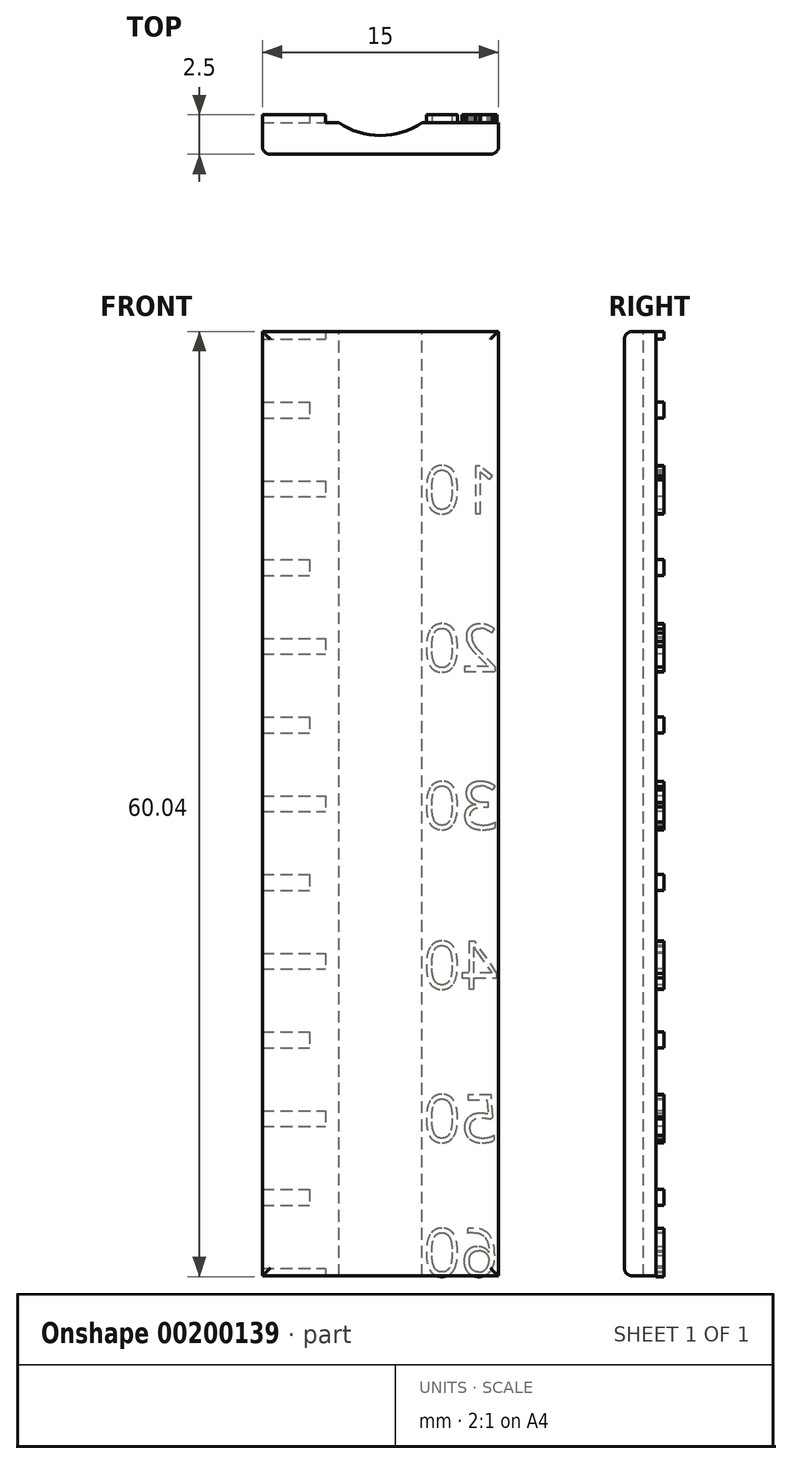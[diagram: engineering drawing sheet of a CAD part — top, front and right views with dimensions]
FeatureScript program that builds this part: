
annotation { "Feature Type Name" : "Feature", "Feature Type Description" : "" }
export const myFeature = defineFeature(function(context is Context, id is Id, definition is map)
    precondition{}
    {
        {
            var Q0;
            Q0=qCreatedBy(makeId("Top.planeOp"),FACE);
            var sketch = newSketch(context, id + "F0", { "sketchPlane" : qUnion([Q0])});
            skLineSegment(sketch, "E0.bottom", {"start": v(0, 0) * mm, "end": v(15, 0) * mm});
            skLineSegment(sketch, "E0.top", {"start": v(0, 2) * mm, "end": v(4.85, 2) * mm});
            skLineSegment(sketch, "E0.left", {"start": v(0, 0) * mm, "end": v(0, 2) * mm});
            skLineSegment(sketch, "E0.right", {"start": v(15, 0) * mm, "end": v(15, 2) * mm});
            skLineSegment(sketch, "E1", {"start": v(7.5, 2) * mm, "end": v(7.5, 5.94) * mm, "construction": true});
            skArc(sketch, "E2", {"start": v(4.85, 2) * mm, "mid": v(7.5, 1.2) * mm, "end": v(10.15, 2) * mm});
            skLineSegment(sketch, "E3.trimOffspring", {"start": v(10.15, 2) * mm, "end": v(15, 2) * mm});
            skSolve(sketch);
        }
        {
            var Q0;
            Q0 = qSketchRegion(id + "F0", true);
            extrude(context, id + "F1", {"entities" : qUnion([Q0]), "oppositeDirection" : true, "depth" : 60 * mm});
        }
        {
            var Q0;
            Q0=makeQuery(id+"F1.opExtrude","SWEPT_FACE",FACE,{"disambiguationData":[OSD([sQuery(id+"F0.wireOp",EDGE,"E0.bottom")])]});
            fillet(context, id + "F2", {"entities" : qUnion([Q0]), "radius" : 0.5 * mm, "tangentPropagation" : true, "allowEdgeOverflow" : false});
        }
        {
            var Q0;
            Q0=makeQuery(id+"F1.opExtrude","SWEPT_FACE",FACE,{"disambiguationData":[OSD([sQuery(id+"F0.wireOp",EDGE,"E0.top")])]});
            var sketch = newSketch(context, id + "F3", { "sketchPlane" : qUnion([Q0])});
            skLineSegment(sketch, "E4.bottom", {"start": v(0, 0) * mm, "end": v(-4, 0) * mm});
            skLineSegment(sketch, "E4.top", {"start": v(0, -0.5) * mm, "end": v(-4, -0.5) * mm});
            skLineSegment(sketch, "E4.left", {"start": v(0, 0) * mm, "end": v(0, -0.5) * mm});
            skLineSegment(sketch, "E4.right", {"start": v(-4, 0) * mm, "end": v(-4, -0.5) * mm});
            skLineSegment(sketch, "E5.bottom", {"start": v(0, -9.5) * mm, "end": v(-4, -9.5) * mm});
            skLineSegment(sketch, "E5.top", {"start": v(0, -10.5) * mm, "end": v(-4, -10.5) * mm});
            skLineSegment(sketch, "E5.left", {"start": v(0, -9.5) * mm, "end": v(0, -10.5) * mm});
            skLineSegment(sketch, "E5.right", {"start": v(-4, -9.5) * mm, "end": v(-4, -10.5) * mm});
            skLineSegment(sketch, "E6.bottom", {"start": v(0, -4.5) * mm, "end": v(-3, -4.5) * mm});
            skLineSegment(sketch, "E6.top", {"start": v(0, -5.5) * mm, "end": v(-3, -5.5) * mm});
            skLineSegment(sketch, "E6.left", {"start": v(0, -4.5) * mm, "end": v(0, -5.5) * mm});
            skLineSegment(sketch, "E6.right", {"start": v(-3, -4.5) * mm, "end": v(-3, -5.5) * mm});
            skLineSegment(sketch, "E7", {"start": v(0, -5) * mm, "end": v(-3, -5) * mm, "construction": true});
            skLineSegment(sketch, "E8", {"start": v(0, -10) * mm, "end": v(-4, -10) * mm, "construction": true});
            skLineSegment(sketch, "E9", {"start": v(-4, 0) * mm, "end": v(-4, -60) * mm, "construction": true});
            skLineSegment(sketch, "E10", {"start": v(-3, -4.5) * mm, "end": v(-3, -60) * mm, "construction": true});
            skLineSegment(sketch, "E11.bottom", {"start": v(0, -14.5) * mm, "end": v(-3, -14.5) * mm});
            skLineSegment(sketch, "E11.top", {"start": v(0, -15.5) * mm, "end": v(-3, -15.5) * mm});
            skLineSegment(sketch, "E11.left", {"start": v(0, -14.5) * mm, "end": v(0, -15.5) * mm});
            skLineSegment(sketch, "E11.right", {"start": v(-3, -14.5) * mm, "end": v(-3, -15.5) * mm});
            skLineSegment(sketch, "E12.bottom", {"start": v(0, -19.5) * mm, "end": v(-4, -19.5) * mm});
            skLineSegment(sketch, "E12.top", {"start": v(0, -20.5) * mm, "end": v(-4, -20.5) * mm});
            skLineSegment(sketch, "E12.left", {"start": v(0, -19.5) * mm, "end": v(0, -20.5) * mm});
            skLineSegment(sketch, "E12.right", {"start": v(-4, -19.5) * mm, "end": v(-4, -20.5) * mm});
            skLineSegment(sketch, "E13.bottom", {"start": v(0, -24.5) * mm, "end": v(-3, -24.5) * mm});
            skLineSegment(sketch, "E13.top", {"start": v(0, -25.5) * mm, "end": v(-3, -25.5) * mm});
            skLineSegment(sketch, "E13.left", {"start": v(0, -24.5) * mm, "end": v(0, -25.5) * mm});
            skLineSegment(sketch, "E13.right", {"start": v(-3, -24.5) * mm, "end": v(-3, -25.5) * mm});
            skLineSegment(sketch, "E14.bottom", {"start": v(0, -29.5) * mm, "end": v(-4, -29.5) * mm});
            skLineSegment(sketch, "E14.top", {"start": v(0, -30.5) * mm, "end": v(-4, -30.5) * mm});
            skLineSegment(sketch, "E14.left", {"start": v(0, -29.5) * mm, "end": v(0, -30.5) * mm});
            skLineSegment(sketch, "E14.right", {"start": v(-4, -29.5) * mm, "end": v(-4, -30.5) * mm});
            skLineSegment(sketch, "E15.bottom", {"start": v(0, -34.5) * mm, "end": v(-3, -34.5) * mm});
            skLineSegment(sketch, "E15.top", {"start": v(0, -35.5) * mm, "end": v(-3, -35.5) * mm});
            skLineSegment(sketch, "E15.left", {"start": v(0, -34.5) * mm, "end": v(0, -35.5) * mm});
            skLineSegment(sketch, "E15.right", {"start": v(-3, -34.5) * mm, "end": v(-3, -35.5) * mm});
            skLineSegment(sketch, "E16.bottom", {"start": v(0, -40.5) * mm, "end": v(-4, -40.5) * mm});
            skLineSegment(sketch, "E16.top", {"start": v(0, -39.5) * mm, "end": v(-4, -39.5) * mm});
            skLineSegment(sketch, "E16.left", {"start": v(0, -39.5) * mm, "end": v(0, -40.5) * mm});
            skLineSegment(sketch, "E16.right", {"start": v(-4, -39.5) * mm, "end": v(-4, -40.5) * mm});
            skLineSegment(sketch, "E17.bottom", {"start": v(0, -44.5) * mm, "end": v(-3, -44.5) * mm});
            skLineSegment(sketch, "E17.top", {"start": v(0, -45.5) * mm, "end": v(-3, -45.5) * mm});
            skLineSegment(sketch, "E17.left", {"start": v(0, -44.5) * mm, "end": v(0, -45.5) * mm});
            skLineSegment(sketch, "E17.right", {"start": v(-3, -44.5) * mm, "end": v(-3, -45.5) * mm});
            skLineSegment(sketch, "E18.bottom", {"start": v(0, -49.5) * mm, "end": v(-4, -49.5) * mm});
            skLineSegment(sketch, "E18.top", {"start": v(0, -50.5) * mm, "end": v(-4, -50.5) * mm});
            skLineSegment(sketch, "E18.left", {"start": v(0, -49.5) * mm, "end": v(0, -50.5) * mm});
            skLineSegment(sketch, "E18.right", {"start": v(-4, -49.5) * mm, "end": v(-4, -50.5) * mm});
            skLineSegment(sketch, "E19.bottom", {"start": v(0, -54.5) * mm, "end": v(-3, -54.5) * mm});
            skLineSegment(sketch, "E19.top", {"start": v(0, -55.5) * mm, "end": v(-3, -55.5) * mm});
            skLineSegment(sketch, "E19.left", {"start": v(0, -54.5) * mm, "end": v(0, -55.5) * mm});
            skLineSegment(sketch, "E19.right", {"start": v(-3, -54.5) * mm, "end": v(-3, -55.5) * mm});
            skLineSegment(sketch, "E20.bottom", {"start": v(0, -59.5) * mm, "end": v(-4, -59.5) * mm});
            skLineSegment(sketch, "E20.top", {"start": v(0, -60) * mm, "end": v(-4, -60) * mm});
            skLineSegment(sketch, "E21", {"start": v(0, -15) * mm, "end": v(-3, -15) * mm, "construction": true});
            skLineSegment(sketch, "E22", {"start": v(0, -20) * mm, "end": v(-4, -20) * mm, "construction": true});
            skLineSegment(sketch, "E23", {"start": v(0, -25) * mm, "end": v(-3, -25) * mm, "construction": true});
            skLineSegment(sketch, "E24", {"start": v(0, -30) * mm, "end": v(-4, -30) * mm, "construction": true});
            skLineSegment(sketch, "E25", {"start": v(0, -35) * mm, "end": v(-3, -35) * mm, "construction": true});
            skLineSegment(sketch, "E26", {"start": v(0, -40) * mm, "end": v(-4, -40) * mm, "construction": true});
            skLineSegment(sketch, "E27", {"start": v(0, -45) * mm, "end": v(-3, -45) * mm, "construction": true});
            skLineSegment(sketch, "E28", {"start": v(0, -50) * mm, "end": v(-4, -50) * mm, "construction": true});
            skLineSegment(sketch, "E29", {"start": v(0, -55) * mm, "end": v(-3, -55) * mm, "construction": true});
            skLineSegment(sketch, "E30", {"start": v(0, -59.5) * mm, "end": v(0, -60) * mm});
            skLineSegment(sketch, "E31", {"start": v(-4, -59.5) * mm, "end": v(-4, -60) * mm});
            skSolve(sketch);
        }
        {
            var Q0;
            Q0 = qSketchRegion(id + "F3", true);
            extrude(context, id + "F4", {"entities" : qUnion([Q0]), "operationType" : NewBodyOperationType.ADD, "depth" : .5 * mm});
        }
        {
            var Q0;
            Q0=makeQuery(id+"F1.opExtrude","SWEPT_FACE",FACE,{"disambiguationData":[OSD([sQuery(id+"F0.wireOp",EDGE,"E3.trimOffspring")])]});
            var sketch = newSketch(context, id + "F5", { "sketchPlane" : qUnion([Q0])});
            skLineSegment(sketch, "E32", {"start": v(-12.57, 0) * mm, "end": v(-12.57, -60) * mm, "construction": true});
            skText(sketch, "E33", { "text": "10", "fontName": "OpenSans-Regular.ttf"});
            skText(sketch, "E34", { "text": "20", "fontName": "OpenSans-Regular.ttf"});
            skText(sketch, "E35", { "text": "30", "fontName": "OpenSans-Regular.ttf"});
            skText(sketch, "E36", { "text": "40", "fontName": "OpenSans-Regular.ttf"});
            skText(sketch, "E37", { "text": "50", "fontName": "OpenSans-Regular.ttf"});
            skText(sketch, "E38", { "text": "60", "fontName": "OpenSans-Regular.ttf"});
            const initialGuessF5  = {"E33": [-0.015, -0.01156, 1, 0, 0.00302], "E34": [-0.015, -0.02161, 1, 0, 0.00302], "E35": [-0.015, -0.03162, 1, 0, 0.00302], "E36": [-0.015, -0.04176, 1, 0, 0.00302], "E37": [-0.015, -0.0515, 1, 0, 0.00302], "E38": [-0.015, -0.06, 1, 0, 0.00302]};
            skSetInitialGuess(sketch, initialGuessF5);
            skSolve(sketch);
        }
        {
            var Q0;
            Q0 = qSketchRegion(id + "F5", true);
            extrude(context, id + "F6", {"entities" : qUnion([Q0]), "operationType" : NewBodyOperationType.ADD, "depth" : .5 * mm});
        }
    });
